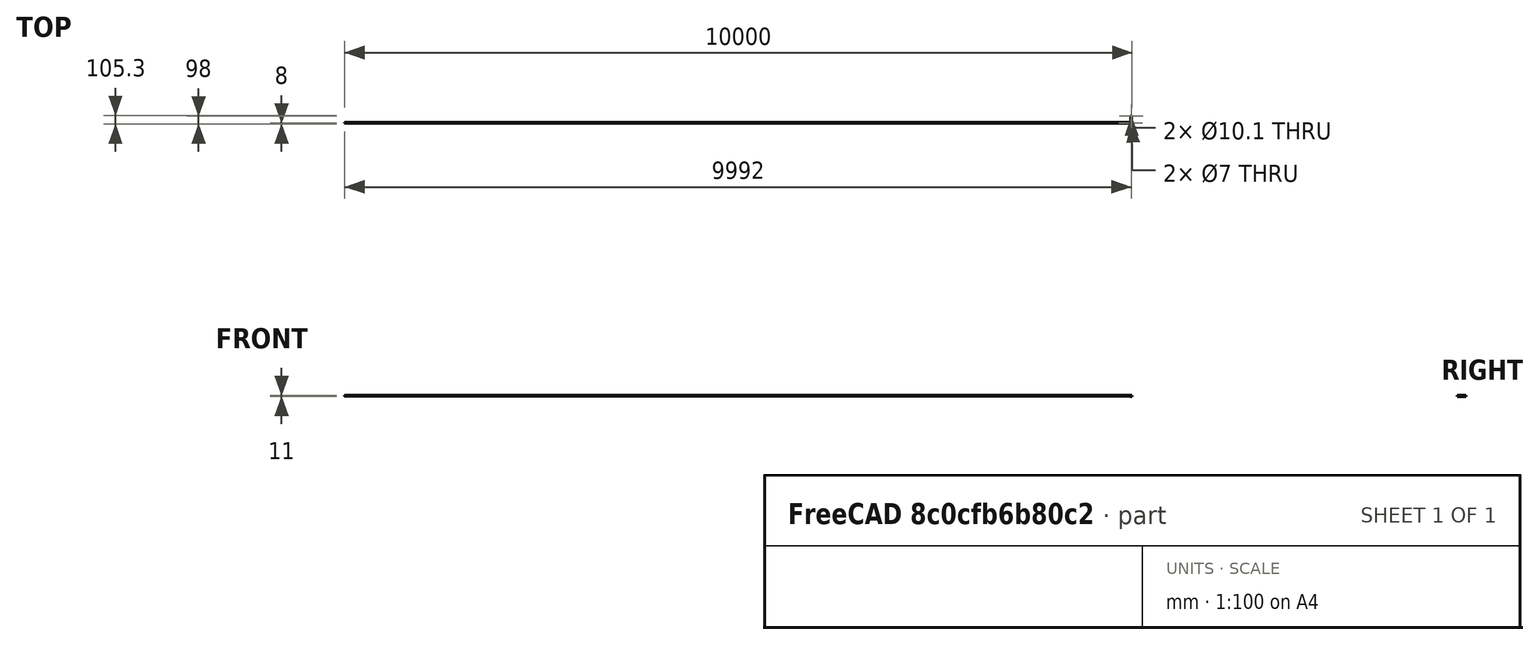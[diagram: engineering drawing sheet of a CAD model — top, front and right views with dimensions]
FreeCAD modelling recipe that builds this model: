
FCSTD DOCUMENT  (FreeCAD 0.16R)
Label: 90mmV2
License: All rights reserved
LicenseURL: http://en.wikipedia.org/wiki/All_rights_reserved
objects: Part::Feature×14, Sketcher::SketchObject×3, PartDesign::Pocket×2, PartDesign::Fillet×2, App::DocumentObjectGroup×1, PartDesign::Pad×1, Mesh::Feature×1
note: 25 computed .brp shape members not serialized (recipe doc carries the construction recipe); baked Part::Feature solids carry a one-line shape summary decoded from their .brp

FEATURE [Part::Feature] Line
  shape: bbox 2e-07 x 9 x 2e-07 mm, 0 faces, 0 solids (baked)
FEATURE [Part::Feature] Line001
  shape: bbox 2e-07 x 9 x 2e-07 mm, 0 faces, 0 solids (baked)
FEATURE [Part::Feature] Line002
  shape: bbox 2e-07 x 57.99 x 2e-07 mm, 0 faces, 0 solids (baked)
FEATURE [Part::Feature] Line003
  shape: bbox 2e-07 x 57.99 x 2e-07 mm, 0 faces, 0 solids (baked)
FEATURE [Part::Feature] Arc
  shape: bbox 16 x 8 x 2e-07 mm, 0 faces, 0 solids (baked)
FEATURE [Part::Feature] Arc001
  shape: bbox 1.883 x 7.277 x 2e-07 mm, 0 faces, 0 solids (baked)
FEATURE [Part::Feature] Arc002
  shape: bbox 1.883 x 7.277 x 2e-07 mm, 0 faces, 0 solids (baked)
FEATURE [Part::Feature] Arc003
  shape: bbox 2.283 x 7.954 x 2e-07 mm, 0 faces, 0 solids (baked)
FEATURE [Part::Feature] Arc004
  shape: bbox 2.283 x 7.954 x 2e-07 mm, 0 faces, 0 solids (baked)
FEATURE [Part::Feature] Arc005
  shape: bbox 1.217 x 4.242 x 2e-07 mm, 0 faces, 0 solids (baked)
FEATURE [Part::Feature] Arc006
  shape: bbox 1.217 x 4.242 x 2e-07 mm, 0 faces, 0 solids (baked)
FEATURE [Part::Feature] Arc007
  shape: bbox 14.6 x 10.84 x 2e-07 mm, 0 faces, 0 solids (baked)
FEATURE [Part::Feature] Circle
  shape: bbox 10.1 x 10.1 x 2e-07 mm, 0 faces, 0 solids (baked)
FEATURE [Part::Feature] Circle001
  shape: bbox 7 x 7 x 2e-07 mm, 0 faces, 0 solids (baked)
FEATURE [App::DocumentObjectGroup] _  label="0"
  Group = -> [Line,Line001,Line002,Line003,Arc,Arc001,Arc002,Arc003,Arc004,Arc005,Arc006,Arc007,Circle,Circle001]
FEATURE [Sketcher::SketchObject] Sketch
  sketch-geometry (14):
    g0: LineSegment StartX=-8 StartY=1.19209e-07 StartZ=0 EndX=-8 EndY=9 EndZ=0
    g1: ArcOfCircle CenterX=-19.5 CenterY=79.1815 CenterZ=0 NormalX=0 NormalY=0 NormalZ=1 Radius=15 StartAngle=0 EndAngle=0.506517
    g2: LineSegment StartX=-4.5 StartY=21.1963 StartZ=0 EndX=-4.5 EndY=79.1815 EndZ=0
    g3: LineSegment StartX=4.5 StartY=21.1963 StartZ=0 EndX=4.5 EndY=79.1815 EndZ=0
    g4: ArcOfCircle CenterX=0 CenterY=0 CenterZ=0 NormalX=0 NormalY=0 NormalZ=1 Radius=8 StartAngle=3.14159 EndAngle=6.28319
    g5: LineSegment StartX=8 StartY=1.19209e-07 StartZ=0 EndX=8 EndY=9 EndZ=0
    g6: ArcOfCircle CenterX=19.5 CenterY=79.1815 CenterZ=0 NormalX=0 NormalY=0 NormalZ=1 Radius=15 StartAngle=2.63508 EndAngle=3.14159
    g7: ArcOfCircle CenterX=19.5 CenterY=21.1963 CenterZ=0 NormalX=0 NormalY=0 NormalZ=1 Radius=15 StartAngle=3.14159 EndAngle=3.70052
    g8: ArcOfCircle CenterX=-19.5 CenterY=21.1963 CenterZ=0 NormalX=0 NormalY=0 NormalZ=1 Radius=15 StartAngle=5.72426 EndAngle=6.28319
    g9: ArcOfCircle CenterX=0 CenterY=9 CenterZ=0 NormalX=0 NormalY=0 NormalZ=1 Radius=8 StartAngle=2.58267 EndAngle=3.14159
    g10: ArcOfCircle CenterX=0 CenterY=9 CenterZ=0 NormalX=0 NormalY=0 NormalZ=1 Radius=8 StartAngle=0 EndAngle=0.558924
    g11: ArcOfCircle CenterX=9.1808e-08 CenterY=90 CenterZ=0 NormalX=0 NormalY=0 NormalZ=1 Radius=7.3 StartAngle=5.77667 EndAngle=9.9313
    g12: Circle CenterX=0 CenterY=0 CenterZ=0 NormalX=0 NormalY=0 NormalZ=1 Radius=5.05
    g13: Circle CenterX=0 CenterY=90 CenterZ=0 NormalX=0 NormalY=0 NormalZ=1 Radius=3.5
  constraints (12):
    c: Coincident(g0,g4)
    c: Coincident(g0,g9)
    c: Coincident(g1,g2)
    c: Coincident(g11,g1)
    c: Coincident(g2,g8)
    c: Coincident(g6,g3)
    c: Coincident(g3,g7)
    c: Coincident(g5,g4)
    c: Coincident(g5,g10)
    c: Coincident(g6,g11)
    c: Coincident(g7,g10)
    c: Coincident(g9,g8)
FEATURE [PartDesign::Pad] Pad
  Length = 11
  Length2 = 100
  Sketch = -> Sketch
  Type = 0
FEATURE [Sketcher::SketchObject] Sketch001
  Placement = pos=(0,0,11) rot=(0,0,1;0rad)
  Support = -> Pad [Face16]
  sketch-geometry (4):
    g0: LineSegment StartX=-22.7683 StartY=109.16 StartZ=0 EndX=26.8694 EndY=109.16 EndZ=0
    g1: LineSegment StartX=26.8694 StartY=109.16 StartZ=0 EndX=26.8694 EndY=18.2423 EndZ=0
    g2: LineSegment StartX=26.8694 StartY=18.2423 StartZ=0 EndX=-22.7683 EndY=18.2423 EndZ=0
    g3: LineSegment StartX=-22.7683 StartY=18.2423 StartZ=0 EndX=-22.7683 EndY=109.16 EndZ=0
  constraints (8):
    c: Coincident(g0,g1)
    c: Coincident(g1,g2)
    c: Coincident(g2,g3)
    c: Coincident(g3,g0)
    c: Horizontal(g0)
    c: Horizontal(g2)
    c: Vertical(g1)
    c: Vertical(g3)
FEATURE [PartDesign::Pocket] Pocket
  Length = 3
  Sketch = -> Sketch001
  Type = 0
FEATURE [PartDesign::Fillet] Fillet
  Base = -> Pocket [Edge48]
  Radius = 2
FEATURE [PartDesign::Fillet] Fillet001
  Base = -> Fillet [Edge20]
  Radius = 0.8
FEATURE [Sketcher::SketchObject] Sketch002
  Placement = pos=(8,0,0) rot=(0.57735,0.57735,0.57735;2.0944rad)
  Support = -> Fillet001 [Face12]
  sketch-geometry (1):
    g0: Circle CenterX=6 CenterY=5.5 CenterZ=0 NormalX=0 NormalY=0 NormalZ=1 Radius=3
  constraints (3):
    c: Radius(g0) = 3
    c: DistanceY(g0) = 5.5
    c: DistanceX(g0) = 6
FEATURE [PartDesign::Pocket] Pocket001
  Length = 5
  Sketch = -> Sketch002
  Type = 1
FEATURE [Mesh::Feature] Mesh  label="Pocket001 (Meshed)"
